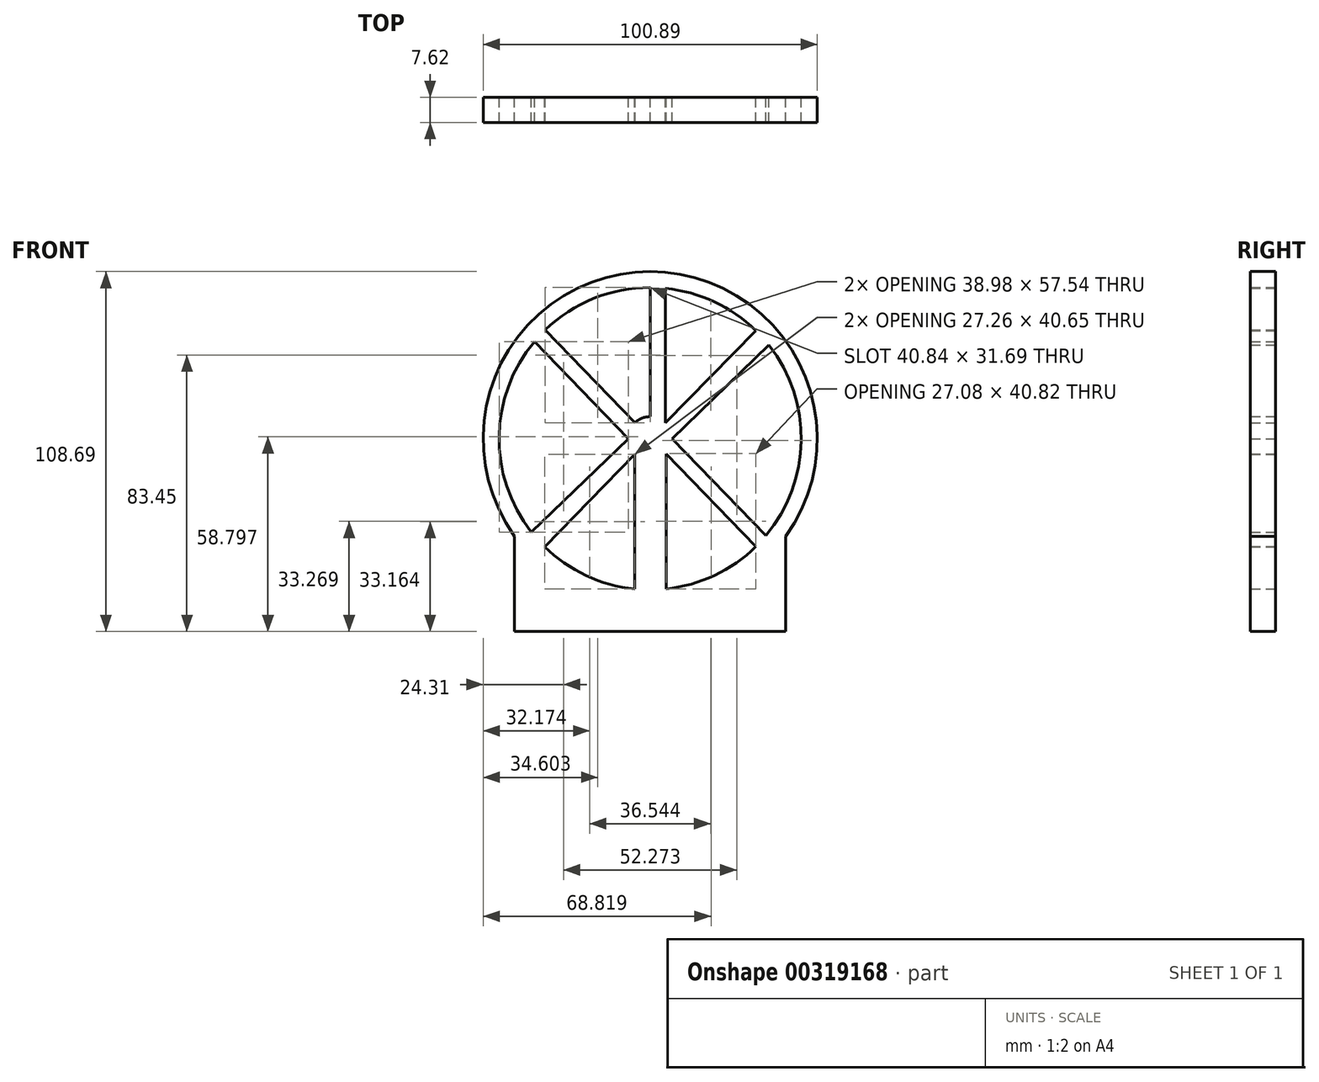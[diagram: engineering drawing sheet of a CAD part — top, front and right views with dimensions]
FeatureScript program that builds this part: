
annotation { "Feature Type Name" : "Feature", "Feature Type Description" : "" }
export const myFeature = defineFeature(function(context is Context, id is Id, definition is map)
    precondition{}
    {
        {
            var Q0;
            Q0=qCreatedBy(makeId("Front.planeOp"),FACE);
            var sketch = newSketch(context, id + "F0", { "sketchPlane" : qUnion([Q0])});
            skCircle(sketch, "E0", {"center": v(-25.51, -9.63) * mm, "radius": 45.63 * mm});
            skCircle(sketch, "E1", {"center": v(-25.51, -9.63) * mm, "radius": 6.64 * mm});
            skLineSegment(sketch, "E2", {"start": v(-20.68, -14.2) * mm, "end": v(-20.68, -55) * mm});
            skLineSegment(sketch, "E3", {"start": v(-30.16, -14.38) * mm, "end": v(-30.16, -55.03) * mm});
            skLineSegment(sketch, "E4", {"start": v(-25.51, -2.99) * mm, "end": v(-25.51, 36) * mm});
            skLineSegment(sketch, "E5", {"start": v(-20.87, -4.88) * mm, "end": v(-20.87, 35.77) * mm});
            skLineSegment(sketch, "E6", {"start": v(-30.12, -4.84) * mm, "end": v(-57.2, 23.2) * mm});
            skLineSegment(sketch, "E7", {"start": v(-32.16, -9.63) * mm, "end": v(-60.47, 19.7) * mm});
            skLineSegment(sketch, "E8", {"start": v(-20.68, -14.2) * mm, "end": v(6.4, -42.25) * mm});
            skLineSegment(sketch, "E9", {"start": v(-20.87, -4.88) * mm, "end": v(6.39, 23) * mm});
            skLineSegment(sketch, "E10", {"start": v(-18.87, -9.63) * mm, "end": v(10.34, 18.6) * mm});
            skLineSegment(sketch, "E11", {"start": v(-30.16, -14.38) * mm, "end": v(-57.41, -42.26) * mm});
            skLineSegment(sketch, "E12", {"start": v(-32.16, -9.63) * mm, "end": v(-61.38, -37.84) * mm});
            skLineSegment(sketch, "E13", {"start": v(-66.46, -29.77) * mm, "end": v(-66.46, -58.98) * mm});
            skLineSegment(sketch, "E14", {"start": v(15.43, -29.77) * mm, "end": v(15.43, -58.98) * mm});
            skLineSegment(sketch, "E15.top", {"start": v(-66.46, -67.87) * mm, "end": v(15.43, -67.87) * mm});
            skLineSegment(sketch, "E15.left", {"start": v(-66.46, -58.98) * mm, "end": v(-66.46, -67.87) * mm});
            skLineSegment(sketch, "E15.right", {"start": v(15.43, -55.21) * mm, "end": v(15.43, -67.87) * mm});
            skCircle(sketch, "E16", {"center": v(-25.51, -9.63) * mm, "radius": 50.45 * mm});
            skLineSegment(sketch, "E17", {"start": v(-18.87, -9.63) * mm, "end": v(9.46, -38.95) * mm});
            skSolve(sketch);
        }
        {
            var Q0;
            Q0 = qSketchRegion(id + "F0", true);
            var Q1;
            {var subQ0=sQuery(id+"F0.wireOp",EDGE,"E6");Q1=makeQuery(id+"F0.imprint","IMPRINT",FACE,{"disambiguationData":[TD([[makeQuery(id+"F0.imprint","IMPRINT",EDGE,{"derivedFrom":subQ0}),1.0]])]});}
            var Q2;
            {var subQ0=sQuery(id+"F0.wireOp",EDGE,"E11");Q2=makeQuery(id+"F0.imprint","IMPRINT",FACE,{"disambiguationData":[TD([[makeQuery(id+"F0.imprint","IMPRINT",EDGE,{"derivedFrom":subQ0}),-1.0]])]});}
            var Q3;
            {var subQ0=sQuery(id+"F0.wireOp",EDGE,"E2");Q3=makeQuery(id+"F0.imprint","IMPRINT",FACE,{"disambiguationData":[TD([[makeQuery(id+"F0.imprint","IMPRINT",EDGE,{"derivedFrom":subQ0}),-1.0]])]});}
            var Q4;
            {var subQ0=sQuery(id+"F0.wireOp",EDGE,"dKv4194F-nrgG-7FGy-9jWl-2zHki8KZIgpp");Q4=makeQuery(id+"F0.imprint","IMPRINT",FACE,{"disambiguationData":[TD([[makeQuery(id+"F0.imprint","IMPRINT",EDGE,{"derivedFrom":subQ0}),-1.0]])]});}
            var Q5;
            {var subQ0=sQuery(id+"F0.wireOp",EDGE,"E9");Q5=makeQuery(id+"F0.imprint","IMPRINT",FACE,{"disambiguationData":[TD([[makeQuery(id+"F0.imprint","IMPRINT",EDGE,{"derivedFrom":subQ0}),-1.0]])]});}
            var Q6;
            {var subQ0=sQuery(id+"F0.wireOp",EDGE,"E4");Q6=makeQuery(id+"F0.imprint","IMPRINT",FACE,{"disambiguationData":[TD([[makeQuery(id+"F0.imprint","IMPRINT",EDGE,{"derivedFrom":subQ0}),-1.0]])]});}
            var Q7;
            {var subQ0=sQuery(id+"F0.wireOp",EDGE,"E1");var subQ3=makeQuery(id+"F0.imprint","INTERSECT",VERTEX,{"derivedFrom":[subQ0,sQuery(id+"F0.wireOp",EDGE,"E4")]});Q7=makeQuery(id+"F0.imprint","IMPRINT",FACE,{"disambiguationData":[TD([[makeQuery(id+"F0.imprint","IMPRINT",EDGE,{"disambiguationData":[TD([[subQ3,-1.0]])],"derivedFrom":subQ0}),1.0]])]});}
            var Q8;
            {var subQ0=sQuery(id+"F0.wireOp",EDGE,"E8");Q8=makeQuery(id+"F0.imprint","IMPRINT",FACE,{"disambiguationData":[TD([[makeQuery(id+"F0.imprint","IMPRINT",EDGE,{"derivedFrom":subQ0}),1.0]])]});}
            extrude(context, id + "F1", {"entities" : qUnion([Q0, Q1, Q2, Q3, Q4, Q5, Q6, Q7, Q8]), "depth" : 7.62 * mm});
        }
    });
